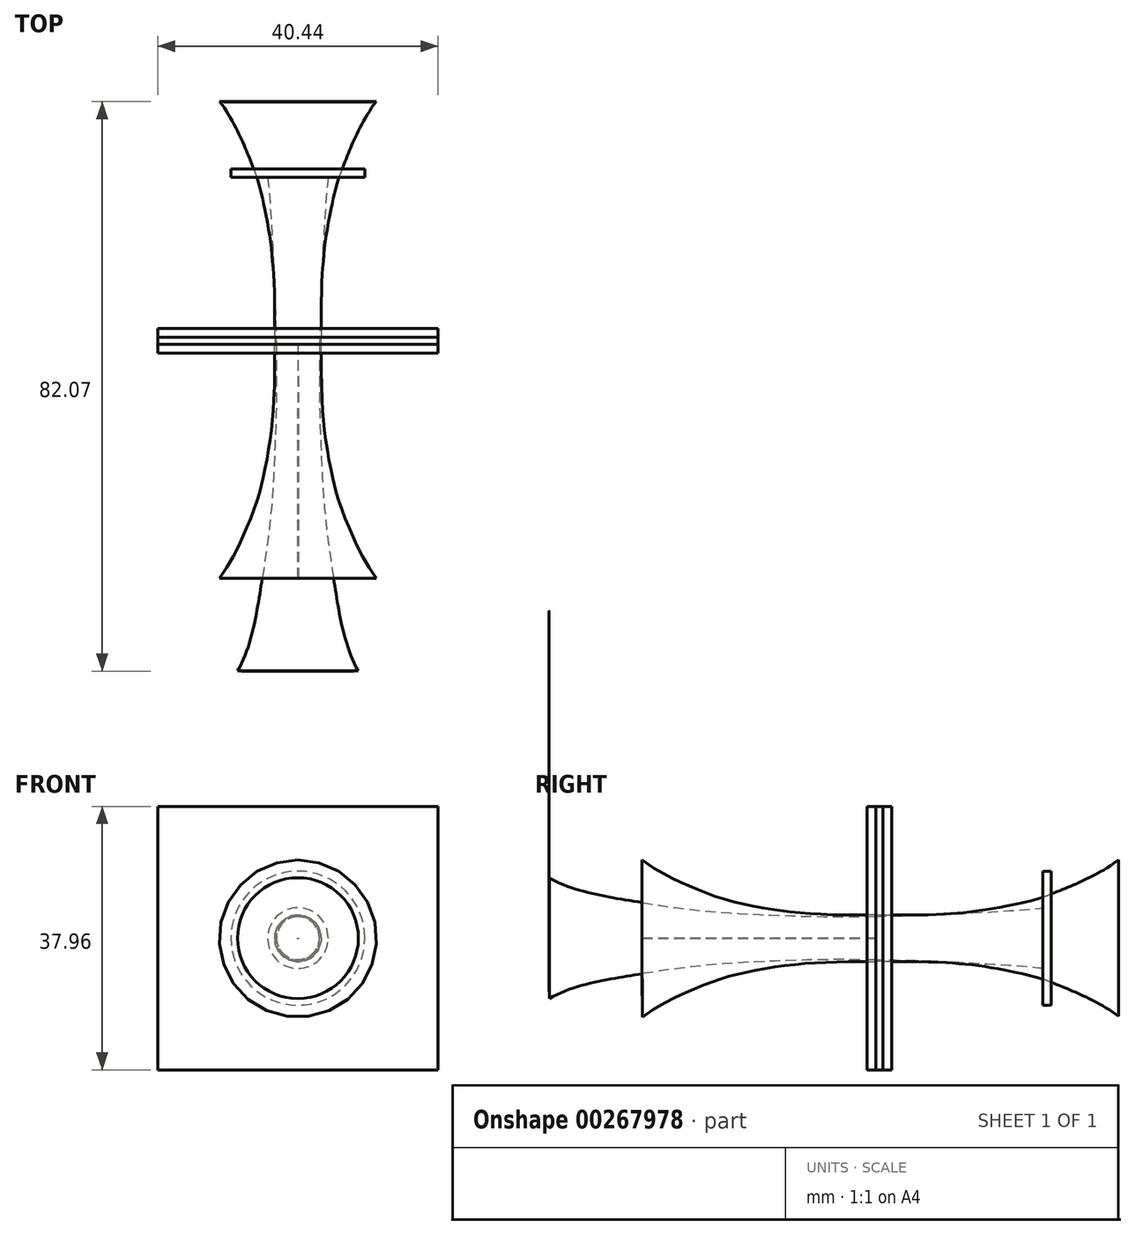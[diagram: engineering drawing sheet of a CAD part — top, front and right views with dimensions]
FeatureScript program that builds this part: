
annotation { "Feature Type Name" : "Feature", "Feature Type Description" : "" }
export const myFeature = defineFeature(function(context is Context, id is Id, definition is map)
    precondition{}
    {
        {
            var Q0;
            Q0=qCreatedBy(makeId("Right.planeOp"),FACE);
            var sketch = newSketch(context, id + "F0", { "sketchPlane" : qUnion([Q0])});
            skFitSpline(sketch, "E0", {"points": [v(-47.07, 8.71) * mm, v(-41.4, 6.56) * mm, v(-34.97, 5.33) * mm, v(-28.67, 4.38) * mm, v(-21.77, 3.68) * mm, v(-12.52, 3.23) * mm, v(0, 3.14) * mm], "startDerivative": vector(31.3, -19.21) * mm, "endDerivative": vector(76.53, 1.48) * mm});
            skLineSegment(sketch, "E1", {"start": v(0, 3.14) * mm, "end": v(0, 0) * mm});
            skLineSegment(sketch, "E2", {"start": v(0, 0) * mm, "end": v(-47.05, 0) * mm});
            skFitSpline(sketch, "E3", {"points": [v(-47.07, 8.71) * mm, v(-47.1, 7.41) * mm, v(-47.1, 6.41) * mm, v(-47.07, 5.03) * mm, v(-47.1, 3.56) * mm, v(-47.07, 1.88) * mm, v(-47.1, 0.57) * mm, v(-47.05, 0) * mm], "startDerivative": vector(-0.5, -26.43) * mm, "endDerivative": vector(0.76, -7.67) * mm});
            skFitSpline(sketch, "E4", {"points": [v(0, 3.14) * mm, v(5.36, 3.27) * mm, v(12.6, 3.56) * mm, v(21.63, 4.13) * mm, v(24.08, 4.37) * mm], "startDerivative": vector(21.24, 0.93) * mm, "endDerivative": vector(12.27, 1.33) * mm});
            skLineSegment(sketch, "E5", {"start": v(24.08, 4.37) * mm, "end": v(24.08, 0) * mm});
            skLineSegment(sketch, "E6", {"start": v(24.08, 0) * mm, "end": v(0, 0) * mm});
            skSolve(sketch);
        }
        {
            var Q0;
            Q0 = qSketchRegion(id + "F0", true);
            var Q1;
            Q1=sQuery(id+"F0.wireOp",EDGE,"E2");
            revolve(context, id + "F1", {"entities" : qUnion([Q0]), "axis" : qUnion([Q1]), "revolveType" : RevolveType.FULL});
        }
        {
            var Q0;
            Q0=qCreatedBy(makeId("Front.planeOp"),FACE);
            var sketch = newSketch(context, id + "F2", { "sketchPlane" : qUnion([Q0])});
            skPoint(sketch, "E7.middle", {"position": v(0, 0) * mm});
            skLineSegment(sketch, "E8.bottom", {"start": v(-20.22, 18.98) * mm, "end": v(20.22, 18.98) * mm});
            skLineSegment(sketch, "E8.top", {"start": v(-20.22, -18.98) * mm, "end": v(20.22, -18.98) * mm});
            skLineSegment(sketch, "E8.left", {"start": v(-20.22, 18.98) * mm, "end": v(-20.22, -18.98) * mm});
            skLineSegment(sketch, "E8.right", {"start": v(20.22, 18.98) * mm, "end": v(20.22, -18.98) * mm});
            skSolve(sketch);
        }
        {
            var Q0;
            Q0 = qSketchRegion(id + "F2", true);
            var Q1;
            Q1=sQuery(id+"F2.wireOp",EDGE,"E7.right");
            var Q2;
            Q2=sQuery(id+"F2.wireOp",EDGE,"E7.bottom");
            var Q3;
            Q3=sQuery(id+"F2.wireOp",EDGE,"E7.top");
            var Q4;
            Q4=sQuery(id+"F2.wireOp",EDGE,"E7.left");
            extrude(context, id + "F3", {"entities" : qUnion([Q0]), "surfaceEntities" : qUnion([Q1, Q2, Q3, Q4]), "offsetDistance" : 25.4 * mm, "depth" : 1.27 * mm});
        }
        {
            var Q0;
            Q0 = qSketchRegion(id + "F2", true);
            extrude(context, id + "F4", {"entities" : qUnion([Q0]), "oppositeDirection" : true, "offsetDistance" : 25.4 * mm, "depth" : 1.02 * mm});
        }
        {
            var Q0;
            Q0 = qSketchRegion(id + "F2", true);
            extrude(context, id + "F5", {"entities" : qUnion([Q0]), "oppositeDirection" : true, "offsetDistance" : 25.4 * mm, "depth" : 2.3 * mm});
        }
        {
            var Q0;
            Q0=makeQuery(id+"F4.opExtrude","SWEPT_BODY",BODY,{"disambiguationData":[OSD([sQuery(id+"F2.wireOp",EDGE,"E8.bottom"),sQuery(id+"F2.wireOp",EDGE,"E8.top"),sQuery(id+"F2.wireOp",EDGE,"E8.left"),sQuery(id+"F2.wireOp",EDGE,"E8.right")])]});
            var Q1;
            Q1=makeQuery(id+"F5.opExtrude","SWEPT_BODY",BODY,{"disambiguationData":[OSD([sQuery(id+"F2.wireOp",EDGE,"E8.bottom"),sQuery(id+"F2.wireOp",EDGE,"E8.top"),sQuery(id+"F2.wireOp",EDGE,"E8.left"),sQuery(id+"F2.wireOp",EDGE,"E8.right")])]});
            booleanBodies(context, id + "F6", {"operationType" : BooleanOperationType.SUBTRACTION, "tools" : qUnion([Q0]), "targets" : qUnion([Q1]), "keepTools" : true});
        }
        {
            var Q0;
            Q0=qCreatedBy(makeId("Front.planeOp"),FACE);
            var sketch = newSketch(context, id + "F7", { "sketchPlane" : qUnion([Q0])});
            skCircle(sketch, "E9", {"center": v(0, 0) * mm, "radius": 3.3 * mm});
            skSolve(sketch);
        }
        {
            var Q0;
            Q0 = qSketchRegion(id + "F7", true);
            extrude(context, id + "F8", {"entities" : qUnion([Q0]), "oppositeDirection" : true, "offsetDistance" : 25.4 * mm, "depth" : 1.02 * mm});
        }
        {
            var Q0;
            Q0=qCreatedBy(makeId("Right.planeOp"),FACE);
            var sketch = newSketch(context, id + "F9", { "sketchPlane" : qUnion([Q0])});
            skLineSegment(sketch, "E10", {"start": v(0, 0) * mm, "end": v(0, 3.34) * mm});
            skFitSpline(sketch, "E11", {"points": [v(0, 3.34) * mm, v(-1.9, 3.34) * mm, v(-4.9, 3.34) * mm, v(-8.29, 3.47) * mm, v(-10.8, 3.64) * mm, v(-13.03, 3.87) * mm, v(-15.09, 4.17) * mm, v(-16.82, 4.47) * mm, v(-19.12, 4.94) * mm, v(-21.26, 5.44) * mm, v(-23.17, 6.04) * mm, v(-25.11, 6.79) * mm, v(-26.94, 7.54) * mm, v(-28.63, 8.29) * mm, v(-30.6, 9.3) * mm, v(-33.71, 11.28) * mm], "startDerivative": vector(-34.28, 0.74) * mm, "endDerivative": vector(-46.61, 35.96) * mm});
            skLineSegment(sketch, "E12", {"start": v(-33.71, 11.28) * mm, "end": v(-33.71, 0) * mm});
            skLineSegment(sketch, "E13", {"start": v(-33.71, 0) * mm, "end": v(0, 0) * mm});
            skLineSegment(sketch, "E14", {"start": v(0, 3.34) * mm, "end": v(0, 0) * mm});
            skLineSegment(sketch, "E15.MirrorCS", {"start": v(1.02, 3.32) * mm, "end": v(1.02, -0.03) * mm});
            skLineSegment(sketch, "E16.MirrorCS", {"start": v(34.95, 11.28) * mm, "end": v(34.95, 0) * mm});
            skLineSegment(sketch, "E17.MirrorCS", {"start": v(34.95, 0) * mm, "end": v(1.02, -0.03) * mm});
            skFitSpline(sketch, "E18.MirrorCS", {"points": [v(1.02, 3.32) * mm, v(3.13, 3.34) * mm, v(6.13, 3.34) * mm, v(9.52, 3.47) * mm, v(12.03, 3.64) * mm, v(14.27, 3.87) * mm, v(16.33, 4.17) * mm, v(18.06, 4.47) * mm, v(20.36, 4.94) * mm, v(22.5, 5.44) * mm, v(24.4, 6.04) * mm, v(26.35, 6.79) * mm, v(28.18, 7.54) * mm, v(29.86, 8.29) * mm, v(31.85, 9.3) * mm, v(34.95, 11.28) * mm], "startDerivative": vector(38, 0) * mm, "endDerivative": vector(46.61, 35.96) * mm});
            skSolve(sketch);
        }
        {
            var Q0;
            Q0 = qSketchRegion(id + "F9", true);
            var Q1;
            Q1=sQuery(id+"F9.wireOp",EDGE,"E17.MirrorCS");
            revolve(context, id + "F10", {"entities" : qUnion([Q0]), "axis" : qUnion([Q1]), "revolveType" : RevolveType.FULL});
        }
        {
            var Q0;
            Q0=qCreatedBy(makeId("Right.planeOp"),FACE);
            var sketch = newSketch(context, id + "F11", { "sketchPlane" : qUnion([Q0])});
            skLineSegment(sketch, "E19.bottom", {"start": v(24.04, 0) * mm, "end": v(25.29, 0) * mm});
            skLineSegment(sketch, "E19.top", {"start": v(24.04, 9.66) * mm, "end": v(25.29, 9.66) * mm});
            skLineSegment(sketch, "E19.left", {"start": v(24.04, 0) * mm, "end": v(24.04, 9.66) * mm});
            skLineSegment(sketch, "E19.right", {"start": v(25.29, 0) * mm, "end": v(25.29, 9.66) * mm});
            skSolve(sketch);
        }
        {
            var Q0;
            Q0 = qSketchRegion(id + "F11", true);
            var Q1;
            Q1=sQuery(id+"F11.wireOp",EDGE,"E19.bottom");
            revolve(context, id + "F12", {"entities" : qUnion([Q0]), "axis" : qUnion([Q1]), "revolveType" : RevolveType.FULL});
        }
    });
